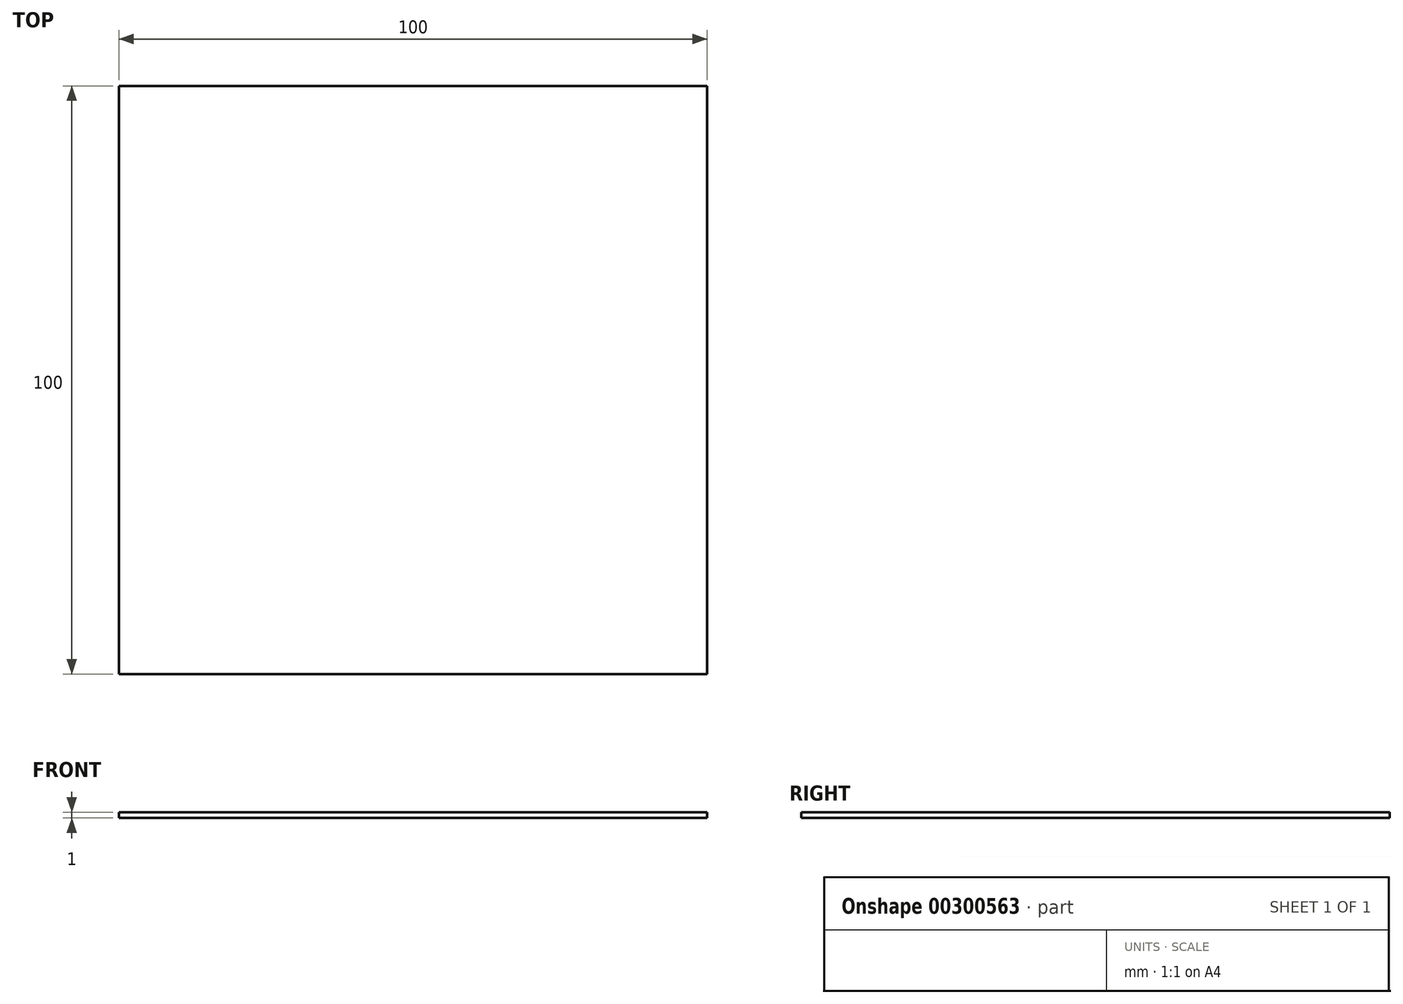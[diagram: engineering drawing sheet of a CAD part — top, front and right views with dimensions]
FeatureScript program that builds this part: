
annotation { "Feature Type Name" : "Feature", "Feature Type Description" : "" }
export const myFeature = defineFeature(function(context is Context, id is Id, definition is map)
    precondition{}
    {
        {
            var Q0;
            Q0=qCreatedBy(makeId("Top.planeOp"),FACE);
            var sketch = newSketch(context, id + "F0", { "sketchPlane" : qUnion([Q0])});
            skLineSegment(sketch, "E0.bottom", {"start": v(50, 50) * mm, "end": v(-50, 50) * mm});
            skLineSegment(sketch, "E0.top", {"start": v(50, -50) * mm, "end": v(-50, -50) * mm});
            skLineSegment(sketch, "E0.left", {"start": v(50, 50) * mm, "end": v(50, -50) * mm});
            skLineSegment(sketch, "E0.right", {"start": v(-50, 50) * mm, "end": v(-50, -50) * mm});
            skSolve(sketch);
        }
        {
            var Q0;
            Q0=makeQuery(id+"F0.imprint","IMPRINT",FACE,{"disambiguationData":[TD([[makeQuery(id+"F0.imprint","IMPRINT",EDGE,{"derivedFrom":sQuery(id+"F0.wireOp",EDGE,"E0.bottom")}),1.0]])]});
            extrude(context, id + "F1", {"entities" : qUnion([Q0]), "depth" : 1 * mm});
        }
    });
